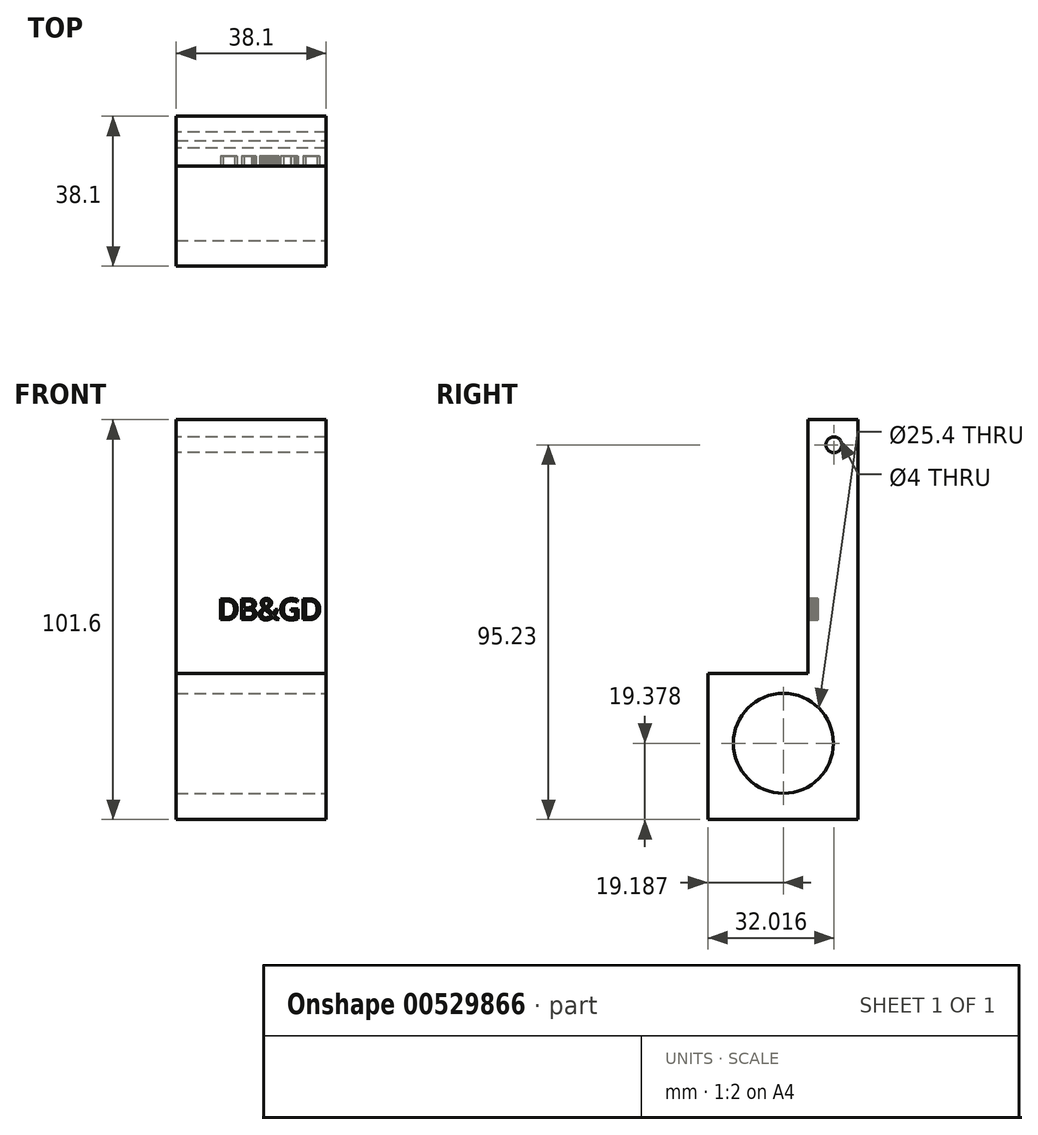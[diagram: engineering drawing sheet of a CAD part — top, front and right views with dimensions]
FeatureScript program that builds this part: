
annotation { "Feature Type Name" : "Feature", "Feature Type Description" : "" }
export const myFeature = defineFeature(function(context is Context, id is Id, definition is map)
    precondition{}
    {
        {
            var Q0;
            Q0=qCreatedBy(makeId("Front.planeOp"),FACE);
            var sketch = newSketch(context, id + "F0", { "sketchPlane" : qUnion([Q0])});
            skLineSegment(sketch, "E0.bottom", {"start": v(19.05, -50.8) * mm, "end": v(-19.05, -50.8) * mm});
            skLineSegment(sketch, "E0.top", {"start": v(19.05, 50.8) * mm, "end": v(-19.05, 50.8) * mm});
            skLineSegment(sketch, "E0.left", {"start": v(19.05, -50.8) * mm, "end": v(19.05, 50.8) * mm});
            skLineSegment(sketch, "E0.right", {"start": v(-19.05, -50.8) * mm, "end": v(-19.05, 50.8) * mm});
            skPoint(sketch, "E0.middle", {"position": v(0, 0) * mm});
            skSolve(sketch);
        }
        {
            var Q0;
            Q0 = qSketchRegion(id + "F0", true);
            extrude(context, id + "F1", {"entities" : qUnion([Q0]), "depth" : 12.7 * mm, "offsetDistance" : 25.4 * mm});
        }
        {
            var Q0;
            Q0=makeQuery(id+"F1.opExtrude","CAP_FACE",FACE,{"disambiguationData":[OSD([sQuery(id+"F0.wireOp",EDGE,"E0.bottom"),sQuery(id+"F0.wireOp",EDGE,"E0.top"),sQuery(id+"F0.wireOp",EDGE,"E0.left"),sQuery(id+"F0.wireOp",EDGE,"E0.right")])],"isStart":false});
            var sketch = newSketch(context, id + "F2", { "sketchPlane" : qUnion([Q0])});
            skLineSegment(sketch, "E1.bottom", {"start": v(19.05, -50.8) * mm, "end": v(-19.05, -50.8) * mm});
            skLineSegment(sketch, "E1.top", {"start": v(19.05, -13.73) * mm, "end": v(-19.05, -13.73) * mm});
            skLineSegment(sketch, "E1.left", {"start": v(19.05, -50.8) * mm, "end": v(19.05, -13.73) * mm});
            skLineSegment(sketch, "E1.right", {"start": v(-19.05, -50.8) * mm, "end": v(-19.05, -13.73) * mm});
            skPoint(sketch, "E1.middle", {"position": v(0, -32.26) * mm});
            skSolve(sketch);
        }
        {
            var Q0;
            Q0 = qSketchRegion(id + "F2", true);
            extrude(context, id + "F3", {"entities" : qUnion([Q0]), "operationType" : NewBodyOperationType.ADD, "depth" : 25.4 * mm, "offsetDistance" : 25.4 * mm});
        }
        {
            var Q0;
            Q0=makeQuery(id+"F3.boolean.opBoolean","MERGE",FACE,{"derivedFrom":[makeQuery(id+"F1.opExtrude","SWEPT_FACE",FACE,{"disambiguationData":[OSD([sQuery(id+"F0.wireOp",EDGE,"E0.left")])]}),makeQuery(id+"F3.opExtrude","SWEPT_FACE",FACE,{"disambiguationData":[OSD([sQuery(id+"F2.wireOp",EDGE,"E1.left")])]})]});
            var sketch = newSketch(context, id + "F4", { "sketchPlane" : qUnion([Q0])});
            skCircle(sketch, "E2", {"center": v(-18.91, -31.42) * mm, "radius": 12.7 * mm});
            skSolve(sketch);
        }
        {
            var Q0;
            Q0 = qSketchRegion(id + "F4", true);
            extrude(context, id + "F5", {"entities" : qUnion([Q0]), "operationType" : NewBodyOperationType.REMOVE, "endBound" : BoundingType.THROUGH_ALL, "oppositeDirection" : true, "depth" : 25.4 * mm, "offsetDistance" : 25.4 * mm});
        }
        {
            var Q0;
            Q0=makeQuery(id+"F1.opExtrude","CAP_FACE",FACE,{"disambiguationData":[OSD([sQuery(id+"F0.wireOp",EDGE,"E0.bottom"),sQuery(id+"F0.wireOp",EDGE,"E0.top"),sQuery(id+"F0.wireOp",EDGE,"E0.left"),sQuery(id+"F0.wireOp",EDGE,"E0.right")])],"isStart":false});
            var sketch = newSketch(context, id + "F6", { "sketchPlane" : qUnion([Q0])});
            skLineSegment(sketch, "E3.bottom", {"start": v(17.78, -2.66) * mm, "end": v(-17.78, -2.66) * mm});
            skLineSegment(sketch, "E3.top", {"start": v(17.78, 48.14) * mm, "end": v(-17.78, 48.14) * mm});
            skLineSegment(sketch, "E3.left", {"start": v(17.78, -2.66) * mm, "end": v(17.78, 48.14) * mm});
            skLineSegment(sketch, "E3.right", {"start": v(-17.78, -2.66) * mm, "end": v(-17.78, 48.14) * mm});
            skPoint(sketch, "E3.middle", {"position": v(0, 22.74) * mm});
            skSolve(sketch);
        }
        {
            var Q0;
            Q0=makeQuery(id+"F3.boolean.opBoolean","MERGE",FACE,{"derivedFrom":[makeQuery(id+"F1.opExtrude","SWEPT_FACE",FACE,{"disambiguationData":[OSD([sQuery(id+"F0.wireOp",EDGE,"E0.right")])]}),makeQuery(id+"F3.opExtrude","SWEPT_FACE",FACE,{"disambiguationData":[OSD([sQuery(id+"F2.wireOp",EDGE,"E1.right")])]})]});
            var sketch = newSketch(context, id + "F7", { "sketchPlane" : qUnion([Q0])});
            skCircle(sketch, "E4", {"center": v(6.08, 44.43) * mm, "radius": 2 * mm});
            skSolve(sketch);
        }
        {
            var Q0;
            Q0 = qSketchRegion(id + "F7", true);
            extrude(context, id + "F8", {"entities" : qUnion([Q0]), "operationType" : NewBodyOperationType.REMOVE, "endBound" : BoundingType.THROUGH_ALL, "oppositeDirection" : true, "depth" : 25.4 * mm, "offsetDistance" : 25.4 * mm});
        }
        {
            var Q0;
            Q0=makeQuery(id+"F6.imprint","IMPRINT",FACE,{"disambiguationData":[TD([[makeQuery(id+"F6.imprint","IMPRINT",EDGE,{"derivedFrom":sQuery(id+"F6.wireOp",EDGE,"E3.bottom")}),-1.0]])]});
            var sketch = newSketch(context, id + "F9", { "sketchPlane" : qUnion([Q0])});
            skText(sketch, "E5", { "text": "DB&GD\n", "fontName": "OpenSans-Regular.ttf"});
            const initialGuessF9  = {"E5": [-0.00855, 0, 1, 0, 0.00533]};
            skSetInitialGuess(sketch, initialGuessF9);
            skSolve(sketch);
        }
        {
            var Q0;
            Q0 = qSketchRegion(id + "F9", true);
            extrude(context, id + "F10", {"entities" : qUnion([Q0]), "operationType" : NewBodyOperationType.REMOVE, "oppositeDirection" : true, "depth" : 2.54 * mm, "offsetDistance" : 25.4 * mm});
        }
    });
